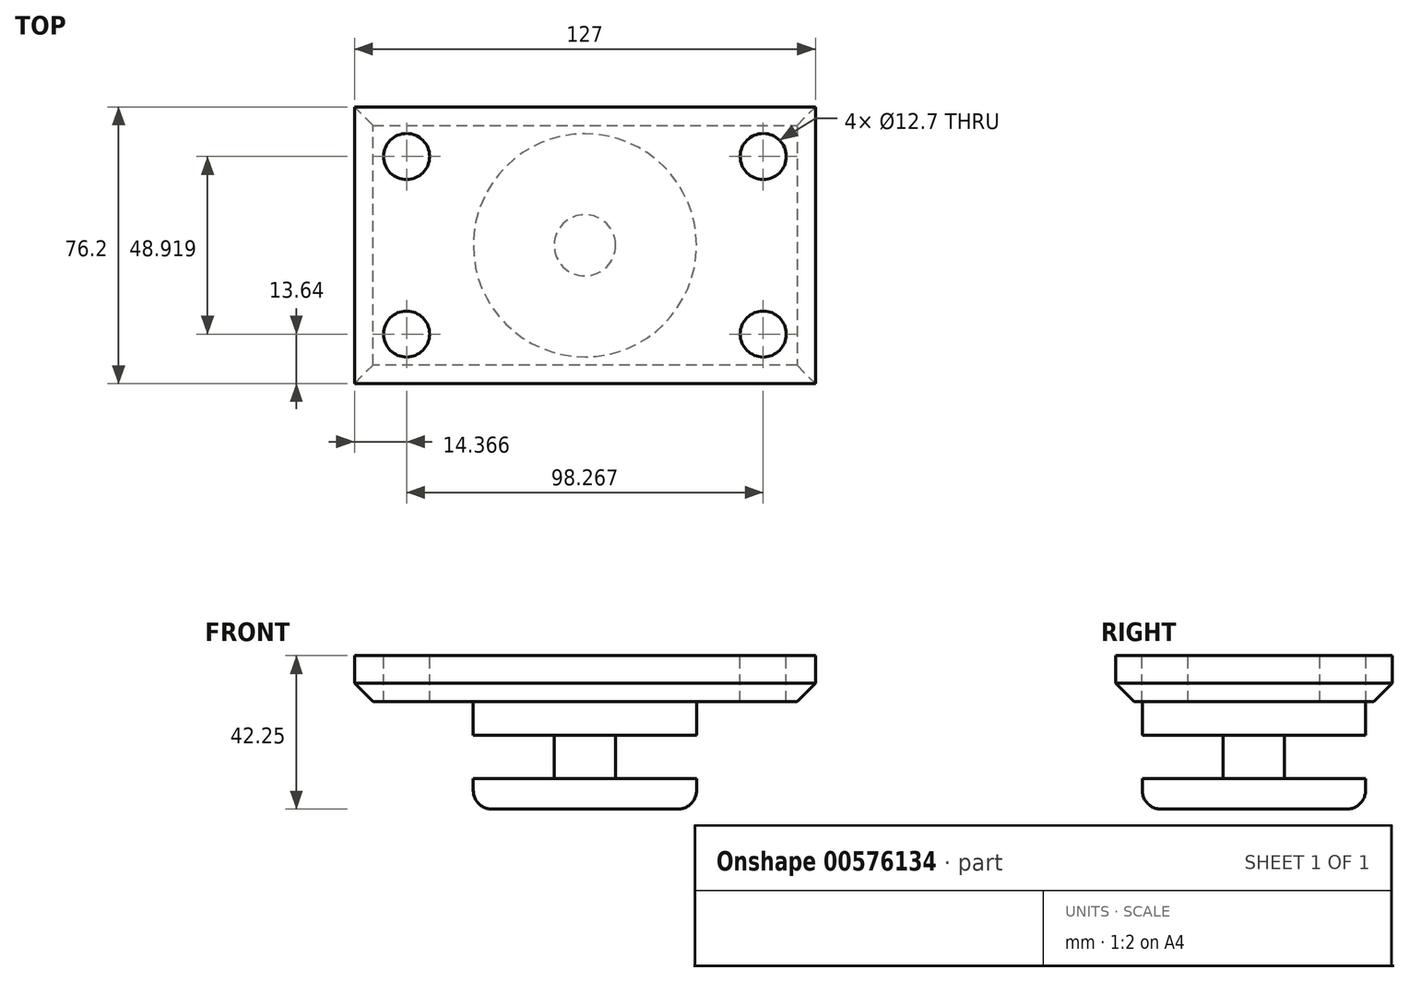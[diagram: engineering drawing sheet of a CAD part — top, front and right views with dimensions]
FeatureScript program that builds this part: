
annotation { "Feature Type Name" : "Feature", "Feature Type Description" : "" }
export const myFeature = defineFeature(function(context is Context, id is Id, definition is map)
    precondition{}
    {
        {
            var Q0;
            Q0=qCreatedBy(makeId("Top.planeOp"),FACE);
            var sketch = newSketch(context, id + "F0", { "sketchPlane" : qUnion([Q0])});
            skLineSegment(sketch, "E0.bottom", {"start": v(-63.5, -38.1) * mm, "end": v(63.5, -38.1) * mm});
            skLineSegment(sketch, "E0.top", {"start": v(-63.5, 38.1) * mm, "end": v(63.5, 38.1) * mm});
            skLineSegment(sketch, "E0.left", {"start": v(-63.5, -38.1) * mm, "end": v(-63.5, 38.1) * mm});
            skLineSegment(sketch, "E0.right", {"start": v(63.5, -38.1) * mm, "end": v(63.5, 38.1) * mm});
            skPoint(sketch, "E0.middle", {"position": v(0, 0) * mm});
            skSolve(sketch);
        }
        {
            var Q0;
            Q0=makeQuery(id+"F0.imprint","IMPRINT",FACE,{"disambiguationData":[TD([[makeQuery(id+"F0.imprint","IMPRINT",EDGE,{"derivedFrom":sQuery(id+"F0.wireOp",EDGE,"E0.bottom")}),1.0]])]});
            extrude(context, id + "F1", {"entities" : qUnion([Q0]), "depth" : 12.7 * mm, "offsetDistance" : 25.4 * mm});
        }
        {
            var Q0;
            Q0=makeQuery(id+"F1.opExtrude","CAP_FACE",FACE,{"disambiguationData":[OSD([sQuery(id+"F0.wireOp",EDGE,"E0.bottom"),sQuery(id+"F0.wireOp",EDGE,"E0.top"),sQuery(id+"F0.wireOp",EDGE,"E0.left"),sQuery(id+"F0.wireOp",EDGE,"E0.right")])],"isStart":false});
            var sketch = newSketch(context, id + "F2", { "sketchPlane" : qUnion([Q0])});
            skLineSegment(sketch, "E1.bottom", {"start": v(49.13, 24.46) * mm, "end": v(-49.13, 24.46) * mm});
            skLineSegment(sketch, "E1.top", {"start": v(49.13, -24.46) * mm, "end": v(-49.13, -24.46) * mm});
            skLineSegment(sketch, "E1.left", {"start": v(49.13, 24.46) * mm, "end": v(49.13, -24.46) * mm});
            skLineSegment(sketch, "E1.right", {"start": v(-49.13, 24.46) * mm, "end": v(-49.13, -24.46) * mm});
            skPoint(sketch, "E1.middle", {"position": v(0, 0) * mm});
            skCircle(sketch, "E2", {"center": v(49.13, 24.46) * mm, "radius": 6.35 * mm});
            skCircle(sketch, "E3", {"center": v(49.13, -24.46) * mm, "radius": 6.35 * mm});
            skCircle(sketch, "E4", {"center": v(-49.13, 24.46) * mm, "radius": 6.35 * mm});
            skCircle(sketch, "E5", {"center": v(-49.13, -24.46) * mm, "radius": 6.35 * mm});
            skSolve(sketch);
        }
        {
            var Q0;
            {var subQ0=sQuery(id+"F2.wireOp",EDGE,"E1.left");var subQ1=sQuery(id+"F2.wireOp",EDGE,"E1.bottom");var subQ2=makeQuery(id+"F2.imprint","INTERSECT",VERTEX,{"derivedFrom":[subQ1,subQ0]});Q0=makeQuery(id+"F2.imprint","IMPRINT",FACE,{"disambiguationData":[TD([[makeQuery(id+"F2.imprint","IMPRINT",EDGE,{"disambiguationData":[TD([[subQ2,-1.0]])],"derivedFrom":subQ1}),-1.0]])]});}
            var Q1;
            {var subQ0=sQuery(id+"F2.wireOp",EDGE,"E1.left");var subQ1=sQuery(id+"F2.wireOp",EDGE,"E1.bottom");var subQ2=makeQuery(id+"F2.imprint","INTERSECT",VERTEX,{"derivedFrom":[subQ1,subQ0]});Q1=makeQuery(id+"F2.imprint","IMPRINT",FACE,{"disambiguationData":[TD([[makeQuery(id+"F2.imprint","IMPRINT",EDGE,{"disambiguationData":[TD([[subQ2,-1.0]])],"derivedFrom":subQ1}),1.0]])]});}
            var Q2;
            {var subQ0=sQuery(id+"F2.wireOp",EDGE,"E1.left");var subQ1=sQuery(id+"F2.wireOp",EDGE,"E1.top");var subQ2=makeQuery(id+"F2.imprint","INTERSECT",VERTEX,{"derivedFrom":[subQ1,subQ0]});Q2=makeQuery(id+"F2.imprint","IMPRINT",FACE,{"disambiguationData":[TD([[makeQuery(id+"F2.imprint","IMPRINT",EDGE,{"disambiguationData":[TD([[subQ2,-1.0]])],"derivedFrom":subQ1}),-1.0]])]});}
            var Q3;
            {var subQ0=sQuery(id+"F2.wireOp",EDGE,"E1.left");var subQ1=sQuery(id+"F2.wireOp",EDGE,"E1.top");var subQ2=makeQuery(id+"F2.imprint","INTERSECT",VERTEX,{"derivedFrom":[subQ1,subQ0]});Q3=makeQuery(id+"F2.imprint","IMPRINT",FACE,{"disambiguationData":[TD([[makeQuery(id+"F2.imprint","IMPRINT",EDGE,{"disambiguationData":[TD([[subQ2,-1.0]])],"derivedFrom":subQ1}),1.0]])]});}
            var Q4;
            {var subQ0=sQuery(id+"F2.wireOp",EDGE,"E1.right");var subQ1=sQuery(id+"F2.wireOp",EDGE,"E1.bottom");var subQ2=makeQuery(id+"F2.imprint","INTERSECT",VERTEX,{"derivedFrom":[subQ1,subQ0]});Q4=makeQuery(id+"F2.imprint","IMPRINT",FACE,{"disambiguationData":[TD([[makeQuery(id+"F2.imprint","IMPRINT",EDGE,{"disambiguationData":[TD([[subQ2,1.0]])],"derivedFrom":subQ1}),1.0]])]});}
            var Q5;
            {var subQ0=sQuery(id+"F2.wireOp",EDGE,"E1.right");var subQ1=sQuery(id+"F2.wireOp",EDGE,"E1.bottom");var subQ2=makeQuery(id+"F2.imprint","INTERSECT",VERTEX,{"derivedFrom":[subQ1,subQ0]});Q5=makeQuery(id+"F2.imprint","IMPRINT",FACE,{"disambiguationData":[TD([[makeQuery(id+"F2.imprint","IMPRINT",EDGE,{"disambiguationData":[TD([[subQ2,1.0]])],"derivedFrom":subQ1}),-1.0]])]});}
            var Q6;
            {var subQ0=sQuery(id+"F2.wireOp",EDGE,"E1.right");var subQ1=sQuery(id+"F2.wireOp",EDGE,"E1.top");var subQ2=makeQuery(id+"F2.imprint","INTERSECT",VERTEX,{"derivedFrom":[subQ1,subQ0]});Q6=makeQuery(id+"F2.imprint","IMPRINT",FACE,{"disambiguationData":[TD([[makeQuery(id+"F2.imprint","IMPRINT",EDGE,{"disambiguationData":[TD([[subQ2,1.0]])],"derivedFrom":subQ1}),-1.0]])]});}
            var Q7;
            {var subQ0=sQuery(id+"F2.wireOp",EDGE,"E1.right");var subQ1=sQuery(id+"F2.wireOp",EDGE,"E1.top");var subQ2=makeQuery(id+"F2.imprint","INTERSECT",VERTEX,{"derivedFrom":[subQ1,subQ0]});Q7=makeQuery(id+"F2.imprint","IMPRINT",FACE,{"disambiguationData":[TD([[makeQuery(id+"F2.imprint","IMPRINT",EDGE,{"disambiguationData":[TD([[subQ2,1.0]])],"derivedFrom":subQ1}),1.0]])]});}
            extrude(context, id + "F3", {"entities" : qUnion([Q0, Q1, Q2, Q3, Q4, Q5, Q6, Q7]), "operationType" : NewBodyOperationType.REMOVE, "endBound" : BoundingType.THROUGH_ALL, "oppositeDirection" : true, "depth" : 25.4 * mm, "offsetDistance" : 25.4 * mm});
        }
        {
            var Q0;
            Q0=qCreatedBy(makeId("Front.planeOp"),FACE);
            var sketch = newSketch(context, id + "F4", { "sketchPlane" : qUnion([Q0])});
            skLineSegment(sketch, "E6.bottom", {"start": v(0, 0) * mm, "end": v(-30.74, 0) * mm});
            skLineSegment(sketch, "E6.top", {"start": v(0, -29.55) * mm, "end": v(-30.74, -29.55) * mm});
            skLineSegment(sketch, "E6.left", {"start": v(0, 0) * mm, "end": v(0, -29.55) * mm});
            skLineSegment(sketch, "E6.right", {"start": v(-30.74, 0) * mm, "end": v(-30.74, -29.55) * mm});
            skSolve(sketch);
        }
        {
            var Q0;
            Q0=makeQuery(id+"F4.imprint","IMPRINT",FACE,{"disambiguationData":[TD([[makeQuery(id+"F4.imprint","IMPRINT",EDGE,{"derivedFrom":sQuery(id+"F4.wireOp",EDGE,"E6.bottom")}),1.0]])]});
            var Q1;
            Q1=sQuery(id+"F4.wireOp",EDGE,"E6.left");
            revolve(context, id + "F5", {"operationType" : NewBodyOperationType.ADD, "entities" : qUnion([Q0]), "axis" : qUnion([Q1]), "revolveType" : RevolveType.FULL});
        }
        {
            var Q0;
            Q0=qCreatedBy(makeId("Right.planeOp"),FACE);
            var sketch = newSketch(context, id + "F6", { "sketchPlane" : qUnion([Q0])});
            skLineSegment(sketch, "E7.bottom", {"start": v(8.45, -9.18) * mm, "end": v(48.68, -9.18) * mm});
            skLineSegment(sketch, "E7.top", {"start": v(8.45, -21.13) * mm, "end": v(48.68, -21.13) * mm});
            skLineSegment(sketch, "E7.left", {"start": v(8.45, -9.18) * mm, "end": v(8.45, -21.13) * mm});
            skLineSegment(sketch, "E7.right", {"start": v(48.68, -9.18) * mm, "end": v(48.68, -21.13) * mm});
            skSolve(sketch);
        }
        {
            var Q0;
            Q0 = qSketchRegion(id + "F6", true);
            var Q1;
            Q1=makeQuery(id+"F5.opRevolve","SWEPT_FACE",FACE,{"disambiguationData":[OSD([sQuery(id+"F4.wireOp",EDGE,"E6.right")])]});
            revolve(context, id + "F7", {"operationType" : NewBodyOperationType.REMOVE, "entities" : qUnion([Q0]), "axis" : qUnion([Q1]), "revolveType" : RevolveType.FULL, "oppositeDirection" : true});
        }
        {
            var Q0;
            Q0=makeQuery(id+"F5.opRevolve","SWEPT_EDGE",EDGE,{"disambiguationData":[OSD([sQuery(id+"F4.wireOp",EDGE,"E6.top"),sQuery(id+"F4.wireOp",EDGE,"E6.right")])]});
            var Q1;
            Q1=makeQuery(id+"F5.opRevolve","SWEPT_EDGE",EDGE,{"disambiguationData":[OSD([sQuery(id+"F4.wireOp",EDGE,"E6.bottom"),sQuery(id+"F4.wireOp",EDGE,"E6.right")])]});
            fillet(context, id + "F8", {"entities" : qUnion([Q0, Q1]), "radius" : 5.08 * mm, "tangentPropagation" : true, "allowEdgeOverflow" : false});
        }
        {
            var Q0;
            Q0=makeQuery(id+"F1.opExtrude","CAP_EDGE",EDGE,{"disambiguationData":[OSD([sQuery(id+"F0.wireOp",EDGE,"E0.top")])],"isStart":true});
            var Q1;
            Q1=makeQuery(id+"F1.opExtrude","CAP_EDGE",EDGE,{"disambiguationData":[OSD([sQuery(id+"F0.wireOp",EDGE,"E0.left")])],"isStart":true});
            var Q2;
            Q2=makeQuery(id+"F1.opExtrude","CAP_EDGE",EDGE,{"disambiguationData":[OSD([sQuery(id+"F0.wireOp",EDGE,"E0.right")])],"isStart":true});
            var Q3;
            Q3=makeQuery(id+"F1.opExtrude","CAP_EDGE",EDGE,{"disambiguationData":[OSD([sQuery(id+"F0.wireOp",EDGE,"E0.bottom")])],"isStart":true});
            chamfer(context, id + "F9", {"entities" : qUnion([Q0, Q1, Q2, Q3]), "width" : 5.08 * mm, "tangentPropagation" : true});
        }
    });
